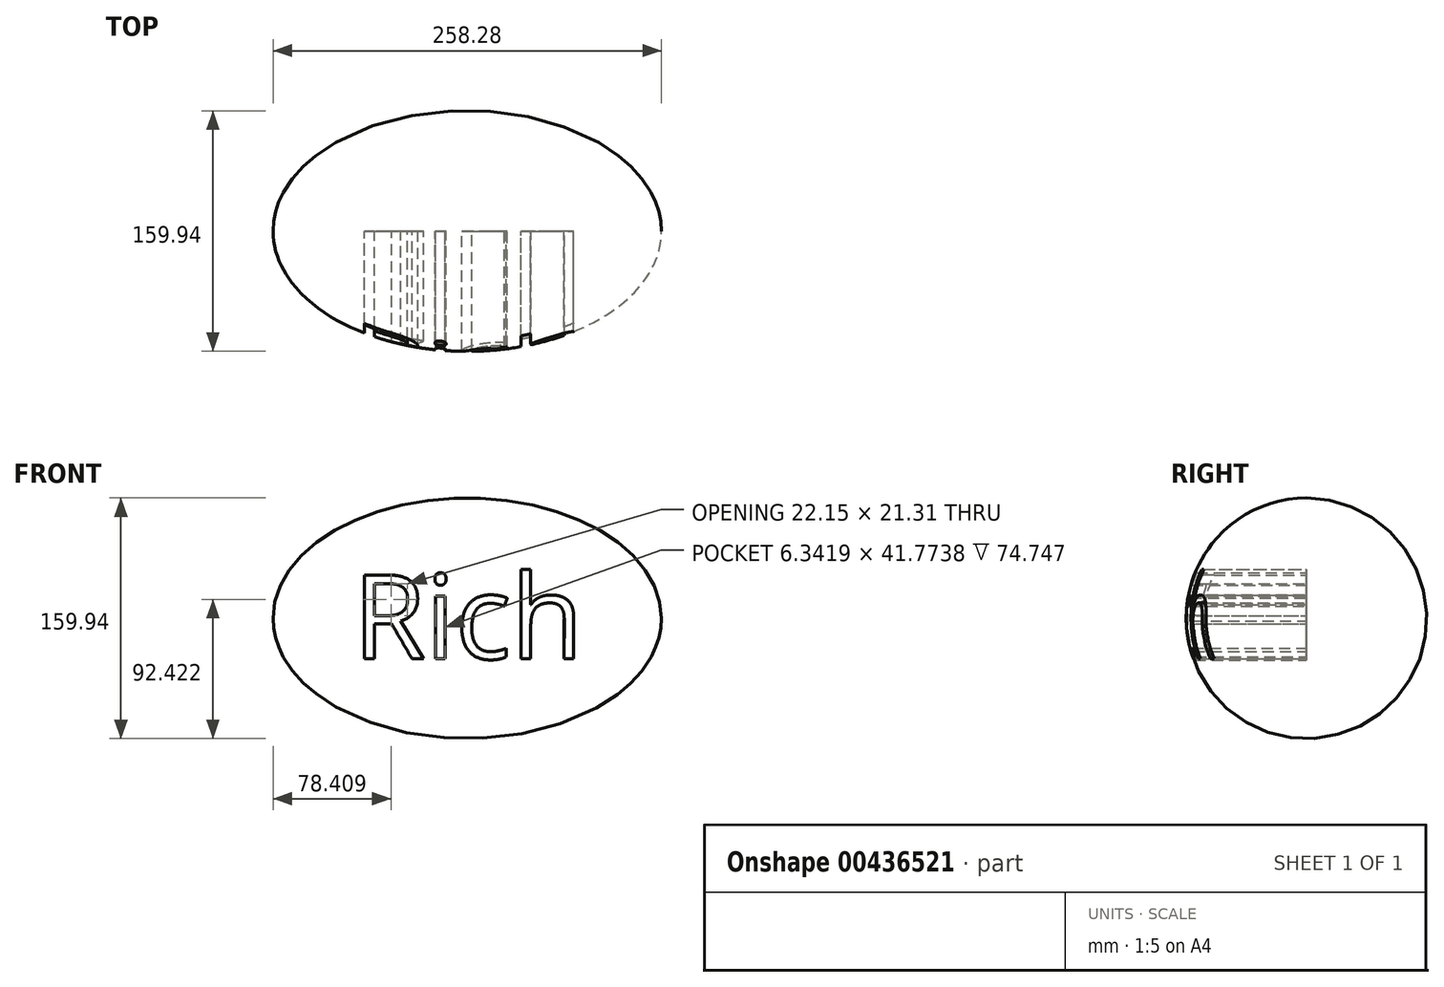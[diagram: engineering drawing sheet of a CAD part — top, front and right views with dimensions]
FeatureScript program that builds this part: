
annotation { "Feature Type Name" : "Feature", "Feature Type Description" : "" }
export const myFeature = defineFeature(function(context is Context, id is Id, definition is map)
    precondition{}
    {
        {
            var Q0;
            Q0=qCreatedBy(makeId("Front.planeOp"),FACE);
            var sketch = newSketch(context, id + "F0", { "sketchPlane" : qUnion([Q0])});
            skEllipse(sketch, "E0", {"center": v(0, 0) * mm, "majorRadius": 129.14 * mm, "minorRadius": 79.97 * mm, "majorAxis": v(1, 0)});
            skLineSegment(sketch, "E1", {"start": v(-129.14, 0) * mm, "end": v(129.14, 0) * mm});
            skSolve(sketch);
        }
        {
            var Q0;
            {var subQ0=sQuery(id+"F0.wireOp",EDGE,"E1");Q0=makeQuery(id+"F0.imprint","IMPRINT",FACE,{"disambiguationData":[TD([[makeQuery(id+"F0.imprint","IMPRINT",EDGE,{"derivedFrom":subQ0}),1.0]])]});}
            var Q1;
            Q1=sQuery(id+"F0.wireOp",EDGE,"E1");
            revolve(context, id + "F1", {"entities" : qUnion([Q0]), "axis" : qUnion([Q1]), "revolveType" : RevolveType.FULL});
        }
        {
            var Q0;
            Q0=qCreatedBy(makeId("Front.planeOp"),FACE);
            var sketch = newSketch(context, id + "F2", { "sketchPlane" : qUnion([Q0])});
            skText(sketch, "E2", { "text": "Rich", "fontName": "OpenSans-Regular.ttf"});
            const initialGuessF2  = {"E2": [-0.07595, -0.02693, 1, -0.00029, 0.0562]};
            skSetInitialGuess(sketch, initialGuessF2);
            skSolve(sketch);
        }
        {
            var Q0;
            Q0 = qSketchRegion(id + "F2", true);
            extrude(context, id + "F3", {"entities" : qUnion([Q0]), "depth" : 226.92 * mm});
        }
        {
            var Q0;
            Q0=makeQuery(id+"F3.opExtrude","SWEPT_BODY",BODY,{"disambiguationData":[OSD([sQuery(id+"F2.wireOp",EDGE,"E2.sketch_text.stroke-45"),sQuery(id+"F2.wireOp",EDGE,"E2.sketch_text.stroke-46"),sQuery(id+"F2.wireOp",EDGE,"E2.sketch_text.stroke-47"),sQuery(id+"F2.wireOp",EDGE,"E2.sketch_text.stroke-48"),sQuery(id+"F2.wireOp",EDGE,"E2.sketch_text.stroke-49"),sQuery(id+"F2.wireOp",EDGE,"E2.sketch_text.stroke-50"),sQuery(id+"F2.wireOp",EDGE,"E2.sketch_text.stroke-51"),sQuery(id+"F2.wireOp",EDGE,"E2.sketch_text.stroke-52"),sQuery(id+"F2.wireOp",EDGE,"E2.sketch_text.stroke-53"),sQuery(id+"F2.wireOp",EDGE,"E2.sketch_text.stroke-54"),sQuery(id+"F2.wireOp",EDGE,"E2.sketch_text.stroke-55"),sQuery(id+"F2.wireOp",EDGE,"E2.sketch_text.stroke-56"),sQuery(id+"F2.wireOp",EDGE,"E2.sketch_text.stroke-57"),sQuery(id+"F2.wireOp",EDGE,"E2.sketch_text.stroke-58"),sQuery(id+"F2.wireOp",EDGE,"E2.sketch_text.stroke-59"),sQuery(id+"F2.wireOp",EDGE,"E2.sketch_text.stroke-60"),sQuery(id+"F2.wireOp",EDGE,"E2.sketch_text.stroke-61"),sQuery(id+"F2.wireOp",EDGE,"E2.sketch_text.stroke-62")])]});
            var Q1;
            Q1=makeQuery(id+"F1.opRevolve","SWEPT_BODY",BODY,{"disambiguationData":[OSD([sQuery(id+"F0.wireOp",EDGE,"E0"),sQuery(id+"F0.wireOp",EDGE,"E1")])]});
            booleanBodies(context, id + "F4", {"operationType" : BooleanOperationType.SUBTRACTION, "tools" : qUnion([Q0]), "targets" : qUnion([Q1])});
        }
        {
            var Q0;
            Q0=makeQuery(id+"F3.opExtrude","SWEPT_BODY",BODY,{"disambiguationData":[OSD([sQuery(id+"F2.wireOp",EDGE,"E2.sketch_text.stroke-30"),sQuery(id+"F2.wireOp",EDGE,"E2.sketch_text.stroke-31"),sQuery(id+"F2.wireOp",EDGE,"E2.sketch_text.stroke-32"),sQuery(id+"F2.wireOp",EDGE,"E2.sketch_text.stroke-33"),sQuery(id+"F2.wireOp",EDGE,"E2.sketch_text.stroke-34"),sQuery(id+"F2.wireOp",EDGE,"E2.sketch_text.stroke-35"),sQuery(id+"F2.wireOp",EDGE,"E2.sketch_text.stroke-36"),sQuery(id+"F2.wireOp",EDGE,"E2.sketch_text.stroke-37"),sQuery(id+"F2.wireOp",EDGE,"E2.sketch_text.stroke-38"),sQuery(id+"F2.wireOp",EDGE,"E2.sketch_text.stroke-39"),sQuery(id+"F2.wireOp",EDGE,"E2.sketch_text.stroke-40"),sQuery(id+"F2.wireOp",EDGE,"E2.sketch_text.stroke-41"),sQuery(id+"F2.wireOp",EDGE,"E2.sketch_text.stroke-42"),sQuery(id+"F2.wireOp",EDGE,"E2.sketch_text.stroke-43"),sQuery(id+"F2.wireOp",EDGE,"E2.sketch_text.stroke-44")])]});
            var Q1;
            Q1=makeQuery(id+"F1.opRevolve","SWEPT_BODY",BODY,{"disambiguationData":[OSD([sQuery(id+"F0.wireOp",EDGE,"E0"),sQuery(id+"F0.wireOp",EDGE,"E1")])]});
            booleanBodies(context, id + "F5", {"operationType" : BooleanOperationType.SUBTRACTION, "tools" : qUnion([Q0]), "targets" : qUnion([Q1])});
        }
        {
            var Q0;
            Q0=makeQuery(id+"F3.opExtrude","SWEPT_BODY",BODY,{"disambiguationData":[OSD([sQuery(id+"F2.wireOp",EDGE,"E2.sketch_text.stroke-18"),sQuery(id+"F2.wireOp",EDGE,"E2.sketch_text.stroke-19"),sQuery(id+"F2.wireOp",EDGE,"E2.sketch_text.stroke-20"),sQuery(id+"F2.wireOp",EDGE,"E2.sketch_text.stroke-21")])]});
            var Q1;
            Q1=makeQuery(id+"F3.opExtrude","SWEPT_BODY",BODY,{"disambiguationData":[OSD([sQuery(id+"F2.wireOp",EDGE,"E2.sketch_text.stroke-0"),sQuery(id+"F2.wireOp",EDGE,"E2.sketch_text.stroke-1"),sQuery(id+"F2.wireOp",EDGE,"E2.sketch_text.stroke-2"),sQuery(id+"F2.wireOp",EDGE,"E2.sketch_text.stroke-3"),sQuery(id+"F2.wireOp",EDGE,"E2.sketch_text.stroke-4"),sQuery(id+"F2.wireOp",EDGE,"E2.sketch_text.stroke-5"),sQuery(id+"F2.wireOp",EDGE,"E2.sketch_text.stroke-6"),sQuery(id+"F2.wireOp",EDGE,"E2.sketch_text.stroke-7"),sQuery(id+"F2.wireOp",EDGE,"E2.sketch_text.stroke-8"),sQuery(id+"F2.wireOp",EDGE,"E2.sketch_text.stroke-9"),sQuery(id+"F2.wireOp",EDGE,"E2.sketch_text.stroke-10"),sQuery(id+"F2.wireOp",EDGE,"E2.sketch_text.stroke-11"),sQuery(id+"F2.wireOp",EDGE,"E2.sketch_text.stroke-12"),sQuery(id+"F2.wireOp",EDGE,"E2.sketch_text.stroke-13"),sQuery(id+"F2.wireOp",EDGE,"E2.sketch_text.stroke-14"),sQuery(id+"F2.wireOp",EDGE,"E2.sketch_text.stroke-15"),sQuery(id+"F2.wireOp",EDGE,"E2.sketch_text.stroke-16"),sQuery(id+"F2.wireOp",EDGE,"E2.sketch_text.stroke-17")])]});
            var Q2;
            Q2=makeQuery(id+"F3.opExtrude","SWEPT_BODY",BODY,{"disambiguationData":[OSD([sQuery(id+"F2.wireOp",EDGE,"E2.sketch_text.stroke-22"),sQuery(id+"F2.wireOp",EDGE,"E2.sketch_text.stroke-23"),sQuery(id+"F2.wireOp",EDGE,"E2.sketch_text.stroke-24"),sQuery(id+"F2.wireOp",EDGE,"E2.sketch_text.stroke-25"),sQuery(id+"F2.wireOp",EDGE,"E2.sketch_text.stroke-26"),sQuery(id+"F2.wireOp",EDGE,"E2.sketch_text.stroke-27"),sQuery(id+"F2.wireOp",EDGE,"E2.sketch_text.stroke-28"),sQuery(id+"F2.wireOp",EDGE,"E2.sketch_text.stroke-29")])]});
            var Q3;
            Q3=makeQuery(id+"F1.opRevolve","SWEPT_BODY",BODY,{"disambiguationData":[OSD([sQuery(id+"F0.wireOp",EDGE,"E0"),sQuery(id+"F0.wireOp",EDGE,"E1")])]});
            booleanBodies(context, id + "F6", {"operationType" : BooleanOperationType.SUBTRACTION, "tools" : qUnion([Q0, Q1, Q2]), "targets" : qUnion([Q3])});
        }
    });
